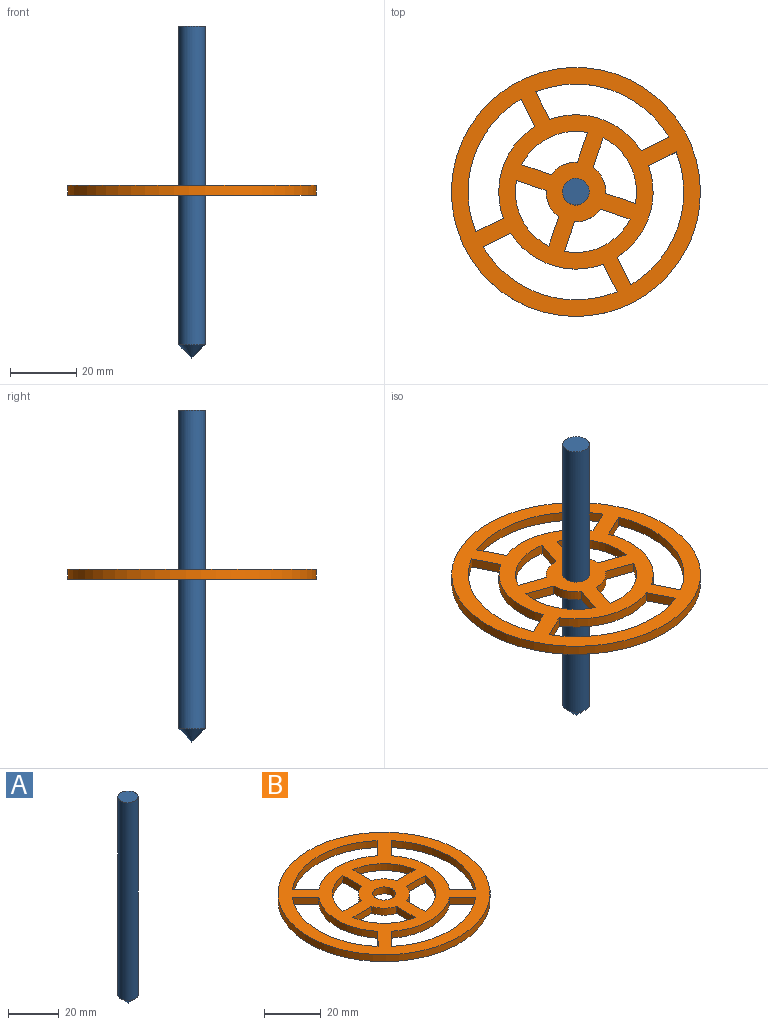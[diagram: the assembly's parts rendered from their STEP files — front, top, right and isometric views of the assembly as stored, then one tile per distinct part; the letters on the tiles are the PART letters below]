
ASSEMBLY  parts=2 mates=1
PART A: 3 faces, bbox 8x8x100 mm
  f0: cylinder r=4mm len=96mm, axis (0,0,-1), area 2412.7mm2, adj f1,f2
  f1: plane 8x8mm, normal (0,0,1), area 50.3mm2, adj f0
  f2: cone r=4mm half-angle=45deg, axis (0,0,1), area 71.1mm2, adj f0
PART B: 36 faces, bbox 75x75x3 mm
  f0: cylinder r=23.25mm len=29.41mm, axis (0,0,-1), area 95.5mm2, adj f1,f33,f34,f35
  f1: plane 6.6x6.53mm, normal (-0.71,0.7,0), area 27.8mm2, adj f0,f2,f34,f35
  f2: cylinder r=32.5mm len=42.58mm, axis (0,0,-1), area 139.3mm2, adj f1,f33,f34,f35
  f3: plane 6.6x6.53mm, normal (-0.71,0.7,0), area 27.8mm2, adj f4,f24,f34,f35
  f4: cylinder r=23.25mm len=29.22mm, axis (0,0,-1), area 94.8mm2, adj f3,f5,f34,f35
  f5: plane 6.57x6.57mm, normal (0.71,0.71,0), area 27.9mm2, adj f4,f24,f34,f35
  f6: plane 9.43x3mm, normal (1,0,0), area 28.3mm2, adj f7,f25,f34,f35
  f7: cylinder r=9mm len=6.15mm, axis (0,0,-1), area 27.2mm2, adj f6,f8,f34,f35
  f8: plane 9.43x3mm, normal (0,-1,0), area 28.3mm2, adj f7,f25,f34,f35
  f9: plane 9.43x3mm, normal (0,-1,0), area 28.3mm2, adj f10,f26,f34,f35
  f10: cylinder r=9mm len=6.15mm, axis (0,0,-1), area 27.2mm2, adj f9,f11,f34,f35
  f11: plane 9.43x3mm, normal (-1,0,0), area 28.3mm2, adj f10,f26,f34,f35
  f12: plane 9.43x3mm, normal (0,1,0), area 28.3mm2, adj f13,f27,f34,f35
  f13: cylinder r=9mm len=6.15mm, axis (0,0,-1), area 27.2mm2, adj f12,f14,f34,f35
  f14: plane 9.43x3mm, normal (1,0,0), area 28.3mm2, adj f13,f27,f34,f35
  f15: plane 6.57x6.57mm, normal (-0.71,-0.71,0), area 27.9mm2, adj f16,f28,f34,f35
  f16: cylinder r=32.5mm len=42.29mm, axis (0,0,-1), area 138.1mm2, adj f15,f17,f34,f35
  f17: plane 6.57x6.57mm, normal (0.71,-0.71,0), area 27.9mm2, adj f16,f28,f34,f35
  f18: plane 6.57x6.57mm, normal (0.71,0.71,0), area 27.9mm2, adj f19,f31,f34,f35
  f19: cylinder r=23.25mm len=29.15mm, axis (0,0,-1), area 94.5mm2, adj f18,f20,f34,f35
  f20: plane 6.57x6.57mm, normal (0.71,-0.71,0), area 27.9mm2, adj f19,f31,f34,f35
  f21: cylinder r=18.25mm len=15.58mm, axis (0,0,-1), area 71mm2, adj f22,f32,f34,f35
  f22: plane 9.43x3mm, normal (-1,0,0), area 28.3mm2, adj f21,f23,f34,f35
  f23: cylinder r=9mm len=6.15mm, axis (0,0,-1), area 27.2mm2, adj f22,f32,f34,f35
  f24: cylinder r=32.5mm len=42.31mm, axis (0,0,-1), area 138.2mm2, adj f3,f5,f34,f35
  f25: cylinder r=18.25mm len=15.58mm, axis (0,0,-1), area 71mm2, adj f6,f8,f34,f35
  f26: cylinder r=18.25mm len=15.58mm, axis (0,0,-1), area 71mm2, adj f9,f11,f34,f35
  f27: cylinder r=18.25mm len=15.58mm, axis (0,0,-1), area 71mm2, adj f12,f14,f34,f35
  f28: cylinder r=23.25mm len=29.15mm, axis (0,0,-1), area 94.5mm2, adj f15,f17,f34,f35
  f29: cylinder r=37.5mm len=75mm, axis (0,0,-1), area 706.9mm2, adj f34,f35
  f30: cylinder r=4mm len=8mm, axis (0,0,-1), area 75.4mm2, adj f34,f35
  f31: cylinder r=32.5mm len=42.29mm, axis (0,0,-1), area 138.1mm2, adj f18,f20,f34,f35
  f32: plane 9.43x3mm, normal (0,1,0), area 28.3mm2, adj f21,f23,f34,f35
  f33: plane 6.57x6.57mm, normal (-0.71,-0.71,0), area 27.9mm2, adj f0,f2,f34,f35
  f34: plane 75x75mm, normal (0,0,1), area 2323.3mm2, adj f0,f1,f2,f3,f4,f5,f6,f7
  f35: plane 75x75mm, normal (0,0,-1), area 2323.3mm2, adj f0,f1,f2,f3,f4,f5,f6,f7
PLACE A at identity fixed
PLACE B rot(axis=(0,0,1),71.2deg) t=(0.23,-0.93,49)mm
MATE revolute A.f0 <-> B.f30  axis (0,0,-1) through (0.23,-0.93,52)mm
